# Revit family: Furniture-Mirror_Cabinet-KOHLER-New_Urbanity-K-99933T-1
name_source: partatom
category: Lighting Fixtures
units: mm (PartAtom-declared; Revit-internal decimal feet)

## family parameters
Cut with Voids When Loaded = No
Host = Face
Light Source = Yes
OmniClass Number = 23.35.47.00
OmniClass Title = Electrical Lighting
Part Type = Normal
Room Calculation Point = No
Round Connector Dimension = Use Diameter
Shared = No

## types (2) — shared parameters
ADA Compliant = No
Apparent Load = 15 VA
Assembly Code = D5040.50
Color Filter = 16777215
Construction Type = Wall Mount
Date Modified = 05/21/2024
Default Elevation = 60"
Depth = 4 7/8"
Dimming Lamp Color Temperature Shift = <None>
Electrical Connector = Yes
Electrical Note = One Dedicated Circuit Required
Emit from Line Length = 10"
Finish = KOHLER-Metal-2BL-Black
Hardware Included = No
Height = 31 15/16"
Lamp = LED
Light Source Symbol Size = 5"
Manufacturer = Kohler Co.
Master Format 2014 = 26 51 13
Master Format 2014 Name = Interior Lighting Fixtures, Lamps, And Ballasts
Material = Premium Metal Construction
Product Documentation Link = https://files.kohler.com.cn
Product Finish = KOHLER-Metal-2BL-Black
Product Name = New Urbanity
Product Page URL = https://www.kohler.com.cn
URL = http://www.kohler.com.cn
Voltage = 12 V
WaterSense Certified = No
Wattage Comments = 15 W
Width = 35 7/16"

## per-type parameters (varying)
| type | Description | Model | Type |
| Left Hinge, NA-Not Applicable | 500 mm - Left | K-99933T-L-NA | 1 |
| Right Hinge, NA-Not Applicable | 500 mm - Right | K-99933T-R-NA | 2 |

## geometry (parser evidence)
native form markers: Sweep x5
no freeform markers — native parametric forms only
